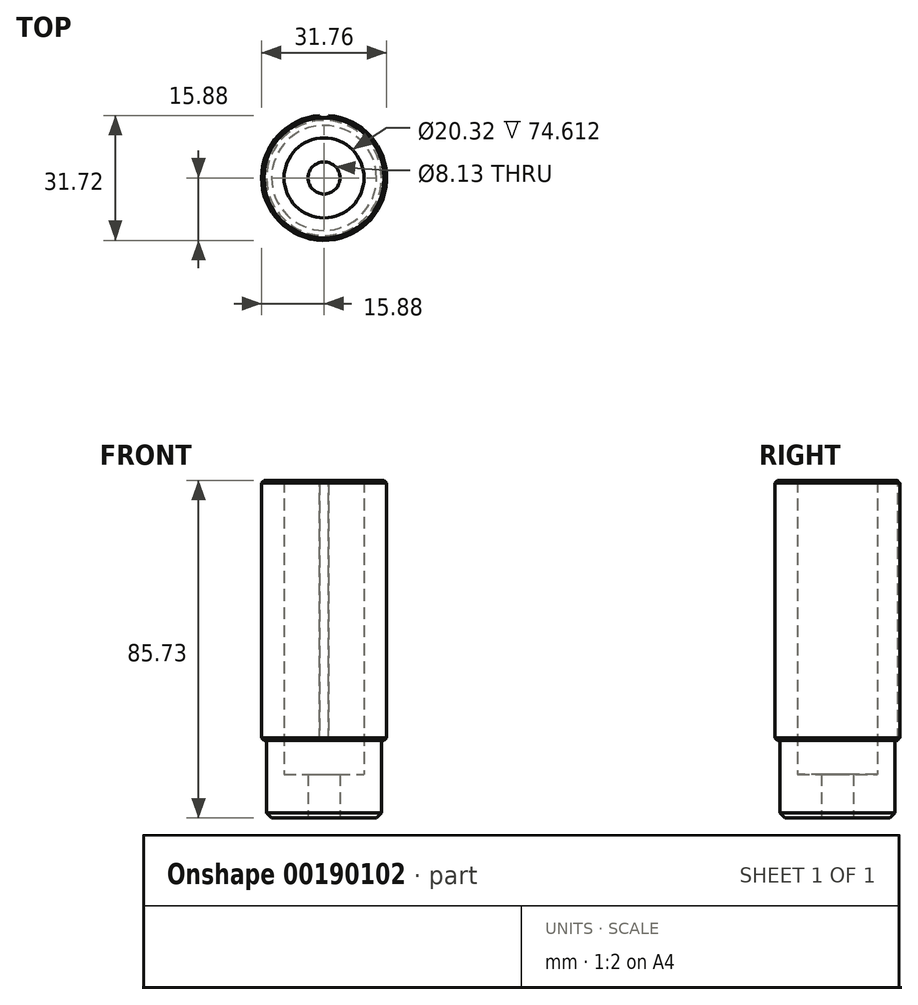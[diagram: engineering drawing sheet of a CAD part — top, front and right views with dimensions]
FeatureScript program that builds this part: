
annotation { "Feature Type Name" : "Feature", "Feature Type Description" : "" }
export const myFeature = defineFeature(function(context is Context, id is Id, definition is map)
    precondition{}
    {
        {
            var Q0;
            Q0=qCreatedBy(makeId("Front.planeOp"),FACE);
            var sketch = newSketch(context, id + "F0", { "sketchPlane" : qUnion([Q0])});
            skLineSegment(sketch, "E0", {"start": v(-10.16, 11.11) * mm, "end": v(-4.06, 11.11) * mm});
            skLineSegment(sketch, "E1", {"start": v(-4.06, 11.11) * mm, "end": v(-4.06, 0) * mm});
            skLineSegment(sketch, "E2", {"start": v(-4.06, 0) * mm, "end": v(-14.6, 0) * mm});
            skLineSegment(sketch, "E3", {"start": v(-14.6, 0) * mm, "end": v(-14.6, 19.69) * mm});
            skLineSegment(sketch, "E4", {"start": v(-14.6, 19.68) * mm, "end": v(-15.88, 19.68) * mm});
            skLineSegment(sketch, "E5", {"start": v(-15.88, 19.68) * mm, "end": v(-15.88, 85.73) * mm});
            skLineSegment(sketch, "E6", {"start": v(-10.16, 85.73) * mm, "end": v(-15.88, 85.73) * mm});
            skLineSegment(sketch, "E7", {"start": v(0, 0) * mm, "end": v(0, 61.9) * mm, "construction": true});
            skLineSegment(sketch, "E8", {"start": v(-10.16, 11.11) * mm, "end": v(-10.16, 85.73) * mm});
            skSolve(sketch);
        }
        {
            var Q0;
            Q0 = qSketchRegion(id + "F0", true);
            var Q1;
            Q1=sQuery(id+"F0.wireOp",EDGE,"E7");
            revolve(context, id + "F1", {"entities" : qUnion([Q0]), "axis" : qUnion([Q1]), "revolveType" : RevolveType.FULL});
        }
        {
            var Q0;
            Q0=makeQuery(id+"F1.opRevolve","SWEPT_FACE",FACE,{"disambiguationData":[OSD([sQuery(id+"F0.wireOp",EDGE,"E6")])]});
            var sketch = newSketch(context, id + "F2", { "sketchPlane" : qUnion([Q0])});
            skLineSegment(sketch, "E9.bottom", {"start": v(-1.08, 16.44) * mm, "end": v(1.08, 16.44) * mm});
            skLineSegment(sketch, "E9.top", {"start": v(-1.08, 15.3) * mm, "end": v(1.08, 15.3) * mm});
            skLineSegment(sketch, "E9.left", {"start": v(-1.08, 16.44) * mm, "end": v(-1.08, 15.3) * mm});
            skLineSegment(sketch, "E9.right", {"start": v(1.08, 16.44) * mm, "end": v(1.08, 15.3) * mm});
            skPoint(sketch, "E9.middle", {"position": v(0, 15.88) * mm});
            skSolve(sketch);
        }
        {
            var Q0;
            Q0=makeQuery(id+"F1.opRevolve","SWEPT_FACE",FACE,{"disambiguationData":[OSD([sQuery(id+"F0.wireOp",EDGE,"E4")])]});
            var sketch = newSketch(context, id + "F3", { "sketchPlane" : qUnion([Q0])});
            skLineSegment(sketch, "E10", {"start": v(-14.6, 6.22) * mm, "end": v(-14.6, 0) * mm});
            skLineSegment(sketch, "E11", {"start": v(0, 0) * mm, "end": v(-32.33, 0) * mm, "construction": true});
            skArc(sketch, "E12.0", {"start": v(-14.6, 6.22) * mm, "mid": v(-15.88, 0) * mm, "end": v(-14.6, -6.22) * mm});
            skLineSegment(sketch, "E13.MirrorCS", {"start": v(-14.6, -6.22) * mm, "end": v(-14.6, 0) * mm});
            skLineSegment(sketch, "E14", {"start": v(0, -0.57) * mm, "end": v(0, 20.93) * mm, "construction": true});
            skArc(sketch, "E15.MirrorCS", {"start": v(14.6, 6.22) * mm, "mid": v(15.88, 0) * mm, "end": v(14.6, -6.22) * mm});
            skLineSegment(sketch, "E16.MirrorCS", {"start": v(14.6, -6.22) * mm, "end": v(14.6, 0) * mm});
            skLineSegment(sketch, "E17.MirrorCS", {"start": v(14.6, 6.22) * mm, "end": v(14.6, 0) * mm});
            skPoint(sketch, "E18.orphan", {"position": v(-14.6, -7.49) * mm});
            skPoint(sketch, "E19.orphan", {"position": v(-13.96, -7.56) * mm});
            skPoint(sketch, "E20.orphan", {"position": v(-14.6, 7.49) * mm});
            skPoint(sketch, "E21.orphan", {"position": v(-13.96, 7.56) * mm});
            skPoint(sketch, "E22.orphan", {"position": v(14.6, -7.49) * mm});
            skPoint(sketch, "E23.orphan", {"position": v(13.96, -7.56) * mm});
            skPoint(sketch, "E24.orphan", {"position": v(14.6, 7.49) * mm});
            skPoint(sketch, "E25.orphan", {"position": v(13.96, 7.56) * mm});
            skSolve(sketch);
        }
        {
            var Q0;
            Q0=makeQuery(id+"F1.opRevolve","SWEPT_EDGE",EDGE,{"disambiguationData":[OSD([sQuery(id+"F0.wireOp",EDGE,"E5"),sQuery(id+"F0.wireOp",EDGE,"E6")])]});
            var Q1;
            {var subQ0=sQuery(id+"F0.wireOp",EDGE,"E4");var subQ1=sQuery(id+"F0.wireOp",EDGE,"E5");Q1=makeQuery(id+"FfgxQThYMJOiaJL_1.boolean.opBoolean","SPLIT",EDGE,{"disambiguationData":[TD([makeQuery(id+"FfgxQThYMJOiaJL_1.opExtrude","SWEPT_FACE",FACE,{"disambiguationData":[OSD([sQuery(id+"F3.wireOp",EDGE,"b7ee4618-6d20-4cac-99f5-459ea11421690.MirrorCS")])]})])],"derivedFrom":makeQuery(id+"F1.opRevolve","SWEPT_EDGE",EDGE,{"disambiguationData":[OSD([subQ0,subQ1])]})});}
            var Q2;
            {var subQ0=sQuery(id+"F0.wireOp",EDGE,"E4");var subQ1=sQuery(id+"F0.wireOp",EDGE,"E5");Q2=makeQuery(id+"FfgxQThYMJOiaJL_1.boolean.opBoolean","SPLIT",EDGE,{"disambiguationData":[TD([makeQuery(id+"FfgxQThYMJOiaJL_1.opExtrude","SWEPT_FACE",FACE,{"disambiguationData":[OSD([sQuery(id+"F3.wireOp",EDGE,"8UvEFoUU-vYyR-qEIX-3m3I-9SLUqBt0WBUS")])]})])],"derivedFrom":makeQuery(id+"F1.opRevolve","SWEPT_EDGE",EDGE,{"disambiguationData":[OSD([subQ0,subQ1])]})});}
            chamfer(context, id + "F4", {"entities" : qUnion([Q0, Q1, Q2]), "width" : 0.64 * mm, "tangentPropagation" : true});
        }
        {
            var Q0;
            Q0 = qSketchRegion(id + "F2", true);
            extrude(context, id + "F5", {"entities" : qUnion([Q0]), "operationType" : NewBodyOperationType.REMOVE, "endBound" : BoundingType.THROUGH_ALL, "oppositeDirection" : true, "depth" : 25.4 * mm});
        }
        {
            var Q0;
            Q0=makeQuery(id+"F1.opRevolve","SWEPT_EDGE",EDGE,{"disambiguationData":[OSD([sQuery(id+"F0.wireOp",EDGE,"E2"),sQuery(id+"F0.wireOp",EDGE,"E3")])]});
            chamfer(context, id + "F6", {"entities" : qUnion([Q0]), "width" : 1.27 * mm, "tangentPropagation" : true});
        }
    });
